# Revit family: Power_Module-Lutron-GRAFIK_Eye-PHPMPA
name_source: partatom
category: Lighting Devices
revit_build: Autodesk Revit 2017 (Build: 20160720_1515(x64)
units: mm (PartAtom-declared; Revit-internal decimal feet)

## family parameters
Always vertical = No
Cut with Voids When Loaded = No
Maintain Annotation Orientation = No
OmniClass Number = 23.85.80.11.27
OmniClass Title = Lighting Controls
Part Type = Normal
Room Calculation Point = No
Round Connector Dimension = Use Diameter
Shared = No
Work Plane-Based = Yes

## types (2) — shared parameters
Assembly Code = D5020
Capacity = 16 A
Control Voltage = 120 V
Default Elevation = 4' - 0"
Description = Phase-Adaptive Power Module
Instruction Sheet Link = http://www.lutron.com
Label = PM
Load Classification = Lighting
Manufacturer = Lutron Electronics Co., Inc
Manufacturer Fax Number = 610-282-1243
Number of Poles = 1
Overall Depth = 0' - 2 13/32"
Overall Height = 0' - 5 3/32"
Overall Width = 0' - 6 5/16"
Performance URL = http://www.lutron.com
Power Module Material = Plastic - Lutron - White
Product Documentation Link = http://www.lutron.com
Product Name = Phase-Adaptive Power Module
Product Page URL = http://www.lutron.com
Series = GRAFIK Eye QS
URL = http://www.lutron.com
Version = 2017 - v1.0b
Video Link = https://www.youtube.com
Warranty URL = http://www.lutron.com
zero-valued in all types: Cost

## per-type parameters (varying)
| type | Load Voltage |
| PHPM-PA-120-WH | 120 V |
| PHPM-PA-DV-WH | 277 V |

note: column(s) folded — value = type name in every type: Model

## geometry (parser evidence)
native form markers: Blend x2, Sweep x3
no freeform markers — native parametric forms only
